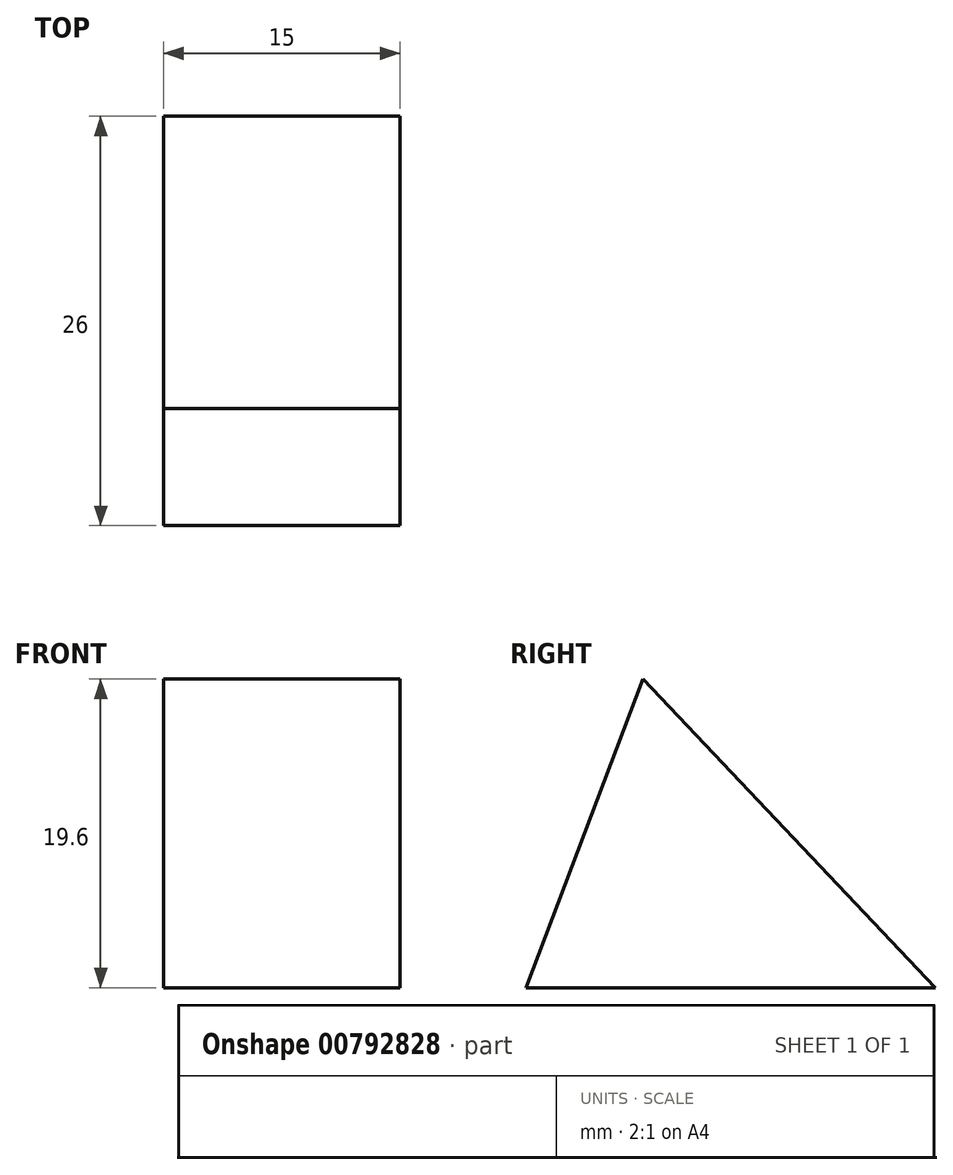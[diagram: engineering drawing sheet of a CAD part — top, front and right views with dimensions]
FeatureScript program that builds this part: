
annotation { "Feature Type Name" : "Feature", "Feature Type Description" : "" }
export const myFeature = defineFeature(function(context is Context, id is Id, definition is map)
    precondition{}
    {
        {
            var Q0;
            Q0=qCreatedBy(makeId("Right.planeOp"), FACE);
            var sketch = newSketch(context, id + "F0", { "sketchPlane" : qUnion([Q0])});
            skLineSegment(sketch, "E0", {"start": v(0, 0) * mm, "end": v(13, 0) * mm});
            skLineSegment(sketch, "E1", {"start": v(0, 13.08) * mm, "end": v(0, -13.57) * mm, "construction": true});
            skLineSegment(sketch, "E2.MirrorCS", {"start": v(0, 0) * mm, "end": v(-13, 0) * mm});
            skLineSegment(sketch, "E3", {"start": v(-13, 0) * mm, "end": v(-5.58, 19.6) * mm});
            skLineSegment(sketch, "E4", {"start": v(-5.58, 19.6) * mm, "end": v(13, 0) * mm});
            skSolve(sketch);
        }
        {
            var Q0;
            Q0 = qSketchRegion(id + "F0", true);
            extrude(context, id + "F1", {"entities" : qUnion([Q0]), "domain" : OperationDomain.MODEL, "flatOperationType" : FlatOperationType.REMOVE, "depth" : 15 * mm, "offsetDistance" : 25 * mm});
        }
    });
